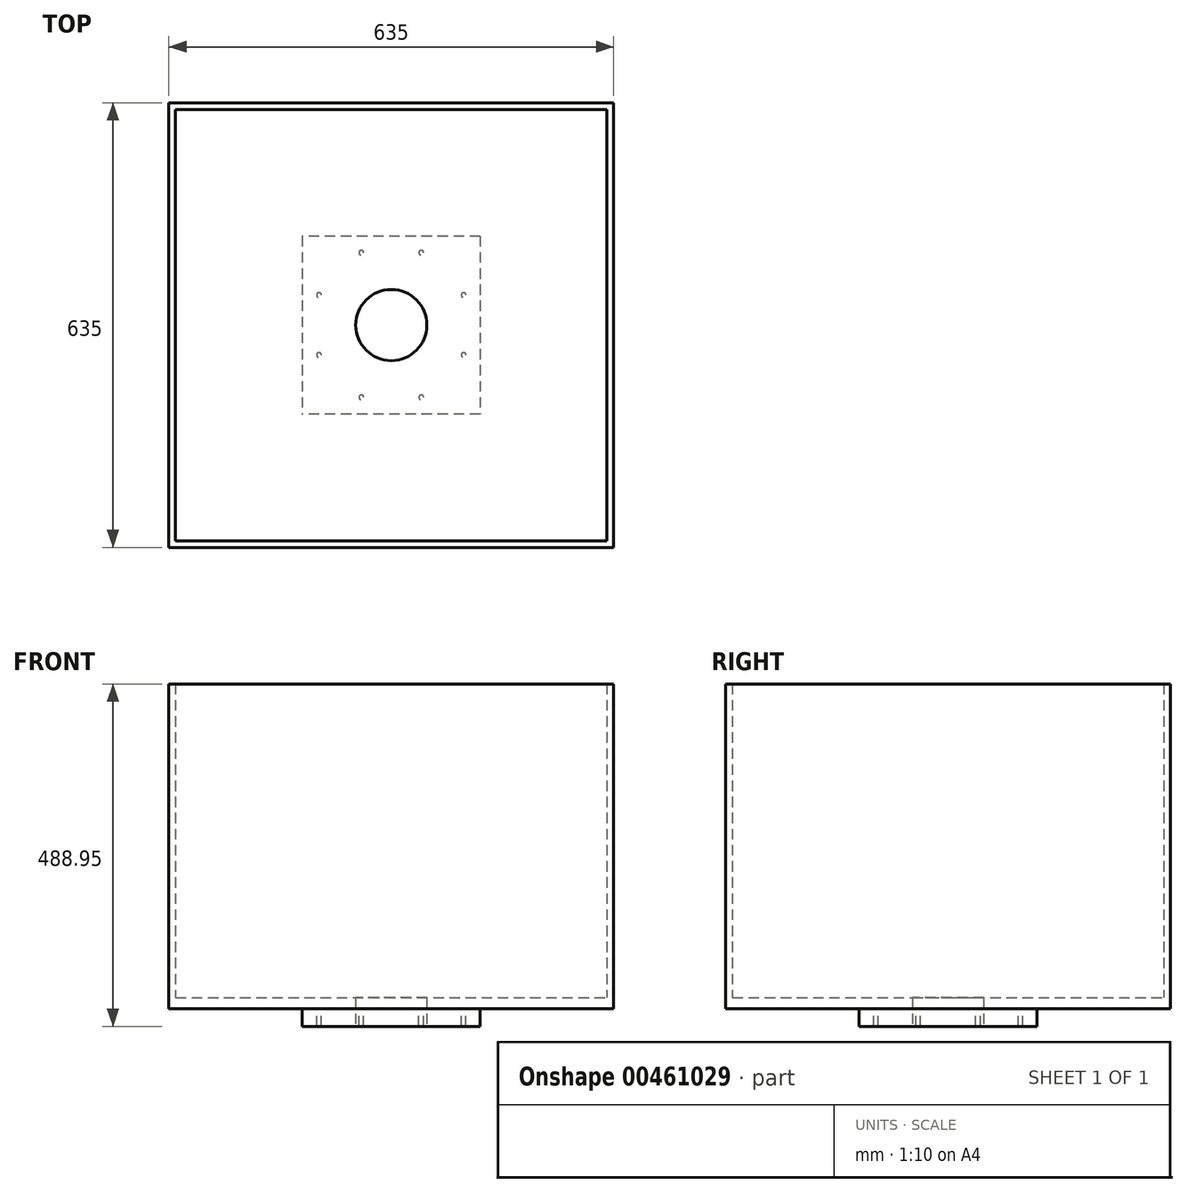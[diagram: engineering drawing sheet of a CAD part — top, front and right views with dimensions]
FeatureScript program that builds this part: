
annotation { "Feature Type Name" : "Feature", "Feature Type Description" : "" }
export const myFeature = defineFeature(function(context is Context, id is Id, definition is map)
    precondition{}
    {
        {
            var Q0;
            Q0=qCreatedBy(makeId("Top.planeOp"),FACE);
            var sketch = newSketch(context, id + "F0", { "sketchPlane" : qUnion([Q0])});
            skLineSegment(sketch, "E0.bottom", {"start": v(0, 0) * mm, "end": v(635, 0) * mm});
            skLineSegment(sketch, "E0.top", {"start": v(0, 635) * mm, "end": v(635, 635) * mm});
            skLineSegment(sketch, "E0.left", {"start": v(0, 0) * mm, "end": v(0, 635) * mm});
            skLineSegment(sketch, "E0.right", {"start": v(635, 0) * mm, "end": v(635, 635) * mm});
            skSolve(sketch);
        }
        {
            var Q0;
            Q0=makeQuery(id+"F0.imprint","IMPRINT",FACE,{"disambiguationData":[TD([[makeQuery(id+"F0.imprint","IMPRINT",EDGE,{"derivedFrom":sQuery(id+"F0.wireOp",EDGE,"E0.bottom")}),1.0]])]});
            extrude(context, id + "F1", {"entities" : qUnion([Q0]), "depth" : 15.88 * mm, "offsetDistance" : 25.4 * mm});
        }
        {
            var Q0;
            Q0=makeQuery(id+"F1.opExtrude","CAP_FACE",FACE,{"disambiguationData":[OSD([sQuery(id+"F0.wireOp",EDGE,"E0.bottom"),sQuery(id+"F0.wireOp",EDGE,"E0.top"),sQuery(id+"F0.wireOp",EDGE,"E0.left"),sQuery(id+"F0.wireOp",EDGE,"E0.right")])],"isStart":false});
            var sketch = newSketch(context, id + "F2", { "sketchPlane" : qUnion([Q0])});
            skLineSegment(sketch, "E1.bottom", {"start": v(0, 0) * mm, "end": v(9.53, 0) * mm});
            skLineSegment(sketch, "E1.top", {"start": v(0, 625.48) * mm, "end": v(9.52, 625.48) * mm});
            skLineSegment(sketch, "E1.left", {"start": v(0, 0) * mm, "end": v(0, 625.48) * mm});
            skLineSegment(sketch, "E1.right", {"start": v(9.53, 0) * mm, "end": v(9.52, 625.48) * mm});
            skLineSegment(sketch, "E2.bottom", {"start": v(0, 625.48) * mm, "end": v(625.48, 625.48) * mm});
            skLineSegment(sketch, "E2.top", {"start": v(0, 635) * mm, "end": v(625.48, 635) * mm});
            skLineSegment(sketch, "E2.left", {"start": v(0, 625.48) * mm, "end": v(0, 635) * mm});
            skLineSegment(sketch, "E2.right", {"start": v(625.48, 625.48) * mm, "end": v(625.48, 635) * mm});
            skLineSegment(sketch, "E3.bottom", {"start": v(625.48, 635) * mm, "end": v(635, 635) * mm});
            skLineSegment(sketch, "E3.top", {"start": v(625.48, 9.52) * mm, "end": v(635, 9.52) * mm});
            skLineSegment(sketch, "E3.left", {"start": v(625.48, 635) * mm, "end": v(625.48, 9.52) * mm});
            skLineSegment(sketch, "E3.right", {"start": v(635, 635) * mm, "end": v(635, 9.52) * mm});
            skLineSegment(sketch, "E4.bottom", {"start": v(635, 9.52) * mm, "end": v(9.52, 9.52) * mm});
            skLineSegment(sketch, "E4.top", {"start": v(635, 0) * mm, "end": v(9.52, 0) * mm});
            skLineSegment(sketch, "E4.left", {"start": v(635, 9.52) * mm, "end": v(635, 0) * mm});
            skLineSegment(sketch, "E4.right", {"start": v(9.52, 9.52) * mm, "end": v(9.52, 0) * mm});
            skSolve(sketch);
        }
        {
            var Q0;
            Q0=makeQuery(id+"F2.imprint","IMPRINT",FACE,{"disambiguationData":[TD([[makeQuery(id+"F2.imprint","IMPRINT",EDGE,{"derivedFrom":sQuery(id+"F2.wireOp",EDGE,"E1.top")}),1.0]])]});
            var Q1;
            {var subQ3=sQuery(id+"F2.wireOp",EDGE,"E1.bottom");Q1=makeQuery(id+"F2.imprint","IMPRINT",FACE,{"disambiguationData":[TD([[makeQuery(id+"F2.imprint","IMPRINT",EDGE,{"derivedFrom":subQ3}),1.0]])]});}
            var Q2;
            Q2=makeQuery(id+"F2.imprint","IMPRINT",FACE,{"disambiguationData":[TD([[makeQuery(id+"F2.imprint","IMPRINT",EDGE,{"derivedFrom":sQuery(id+"F2.wireOp",EDGE,"E3.top")}),-1.0]])]});
            var Q3;
            Q3=makeQuery(id+"F2.imprint","IMPRINT",FACE,{"disambiguationData":[TD([[makeQuery(id+"F2.imprint","IMPRINT",EDGE,{"derivedFrom":sQuery(id+"F2.wireOp",EDGE,"E2.right")}),-1.0]])]});
            extrude(context, id + "F3", {"entities" : qUnion([Q0, Q1, Q2, Q3]), "operationType" : NewBodyOperationType.ADD, "depth" : 447.67 * mm, "offsetDistance" : 25.4 * mm});
        }
        {
            var Q0;
            Q0=makeQuery(id+"F1.opExtrude","CAP_FACE",FACE,{"disambiguationData":[OSD([sQuery(id+"F0.wireOp",EDGE,"E0.bottom"),sQuery(id+"F0.wireOp",EDGE,"E0.top"),sQuery(id+"F0.wireOp",EDGE,"E0.left"),sQuery(id+"F0.wireOp",EDGE,"E0.right")])],"isStart":true});
            var sketch = newSketch(context, id + "F4", { "sketchPlane" : qUnion([Q0])});
            skCircle(sketch, "E5", {"center": v(317.5, -317.5) * mm, "radius": 50.8 * mm});
            skPoint(sketch, "E5.centerSnap0", {"position": v(317.5, -635) * mm});
            skPoint(sketch, "E5.centerSnap1", {"position": v(0, -317.5) * mm});
            skSolve(sketch);
        }
        {
            var Q0;
            Q0=makeQuery(id+"F4.imprint","IMPRINT",FACE,{"disambiguationData":[TD([[makeQuery(id+"F4.imprint","IMPRINT",EDGE,{"derivedFrom":sQuery(id+"F4.wireOp",EDGE,"E5")}),1.0]])]});
            extrude(context, id + "F5", {"entities" : qUnion([Q0]), "operationType" : NewBodyOperationType.REMOVE, "endBound" : BoundingType.SYMMETRIC, "oppositeDirection" : true, "depth" : 50.8 * mm, "offsetDistance" : 25.4 * mm});
        }
        {
            var Q0;
            Q0=makeQuery(id+"F1.opExtrude","CAP_FACE",FACE,{"disambiguationData":[OSD([sQuery(id+"F0.wireOp",EDGE,"E0.bottom"),sQuery(id+"F0.wireOp",EDGE,"E0.top"),sQuery(id+"F0.wireOp",EDGE,"E0.left"),sQuery(id+"F0.wireOp",EDGE,"E0.right")])],"isStart":true});
            var sketch = newSketch(context, id + "F6", { "sketchPlane" : qUnion([Q0])});
            skLineSegment(sketch, "E6.bottom", {"start": v(444.5, -444.5) * mm, "end": v(190.5, -444.5) * mm});
            skLineSegment(sketch, "E6.top", {"start": v(444.5, -190.5) * mm, "end": v(190.5, -190.5) * mm});
            skLineSegment(sketch, "E6.left", {"start": v(444.5, -444.5) * mm, "end": v(444.5, -190.5) * mm});
            skLineSegment(sketch, "E6.right", {"start": v(190.5, -444.5) * mm, "end": v(190.5, -190.5) * mm});
            skCircle(sketch, "E7", {"center": v(360.27, -214.25) * mm, "radius": 3.4 * mm});
            skCircle(sketch, "E8.1.0", {"center": v(274.73, -214.25) * mm, "radius": 3.4 * mm});
            skCircle(sketch, "E8.2.0", {"center": v(214.25, -274.73) * mm, "radius": 3.4 * mm});
            skCircle(sketch, "E8.3.0", {"center": v(214.25, -360.27) * mm, "radius": 3.4 * mm});
            skCircle(sketch, "E8.4.0", {"center": v(274.73, -420.75) * mm, "radius": 3.4 * mm});
            skCircle(sketch, "E8.5.0", {"center": v(360.27, -420.75) * mm, "radius": 3.4 * mm});
            skCircle(sketch, "E8.6.0", {"center": v(420.75, -360.27) * mm, "radius": 3.4 * mm});
            skCircle(sketch, "E8.7.0", {"center": v(420.75, -274.73) * mm, "radius": 3.4 * mm});
            skPoint(sketch, "E8.center", {"position": v(317.5, -317.5) * mm});
            skCircle(sketch, "E9", {"center": v(317.5, -317.5) * mm, "radius": 101.6 * mm, "construction": true});
            skCircle(sketch, "E10", {"center": v(317.5, -317.5) * mm, "radius": 93.66 * mm, "construction": true});
            skLineSegment(sketch, "E11", {"start": v(219.31, -214.25) * mm, "end": v(428.2, -214.25) * mm});
            skSolve(sketch);
        }
        {
            var Q0;
            Q0=makeQuery(id+"F6.imprint","IMPRINT",FACE,{"disambiguationData":[TD([[makeQuery(id+"F6.imprint","IMPRINT",EDGE,{"derivedFrom":sQuery(id+"F6.wireOp",EDGE,"E6.bottom")}),-1.0]])]});
            extrude(context, id + "F7", {"entities" : qUnion([Q0]), "operationType" : NewBodyOperationType.ADD, "depth" : 25.4 * mm, "offsetDistance" : 25.4 * mm});
        }
    });
